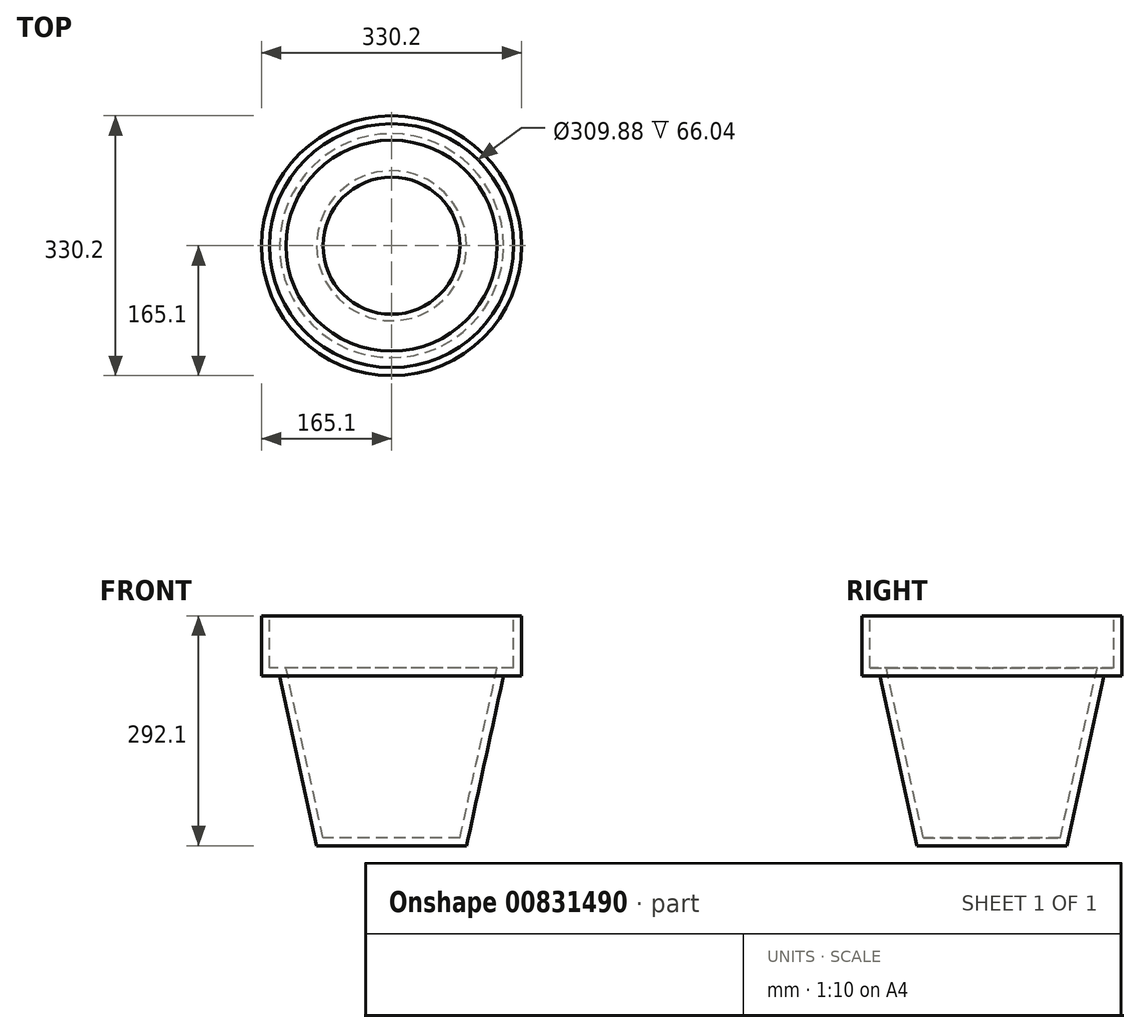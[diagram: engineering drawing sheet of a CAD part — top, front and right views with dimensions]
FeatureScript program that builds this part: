
annotation { "Feature Type Name" : "Feature", "Feature Type Description" : "" }
export const myFeature = defineFeature(function(context is Context, id is Id, definition is map)
    precondition{}
    {
        {
            var Q0;
            Q0=qCreatedBy(makeId("Front.planeOp"),FACE);
            var sketch = newSketch(context, id + "F0", { "sketchPlane" : qUnion([Q0])});
            skLineSegment(sketch, "E0", {"start": v(0, 0) * mm, "end": v(95.25, 0) * mm});
            skLineSegment(sketch, "E1", {"start": v(95.25, 0) * mm, "end": v(142.24, 215.9) * mm});
            skLineSegment(sketch, "E2", {"start": v(142.24, 215.9) * mm, "end": v(165.1, 215.9) * mm});
            skLineSegment(sketch, "E3", {"start": v(165.1, 215.9) * mm, "end": v(165.1, 292.1) * mm});
            skLineSegment(sketch, "E4", {"start": v(165.1, 292.1) * mm, "end": v(0, 292.1) * mm});
            skLineSegment(sketch, "E5", {"start": v(0, 292.1) * mm, "end": v(0, 0) * mm});
            skSolve(sketch);
        }
        {
            var Q0;
            Q0 = qSketchRegion(id + "F0", true);
            var Q1;
            Q1=sQuery(id+"F0.wireOp",EDGE,"E5");
            revolve(context, id + "F1", {"surfaceOperationType" : NewSurfaceOperationType.NEW, "entities" : qUnion([Q0]), "axis" : qUnion([Q1]), "revolveType" : RevolveType.FULL});
        }
        {
            var Q0;
            Q0=makeQuery(id+"F1.opRevolve","SWEPT_FACE",FACE,{"disambiguationData":[OSD([sQuery(id+"F0.wireOp",EDGE,"E4")])]});
            shell(context, id + "F2", {"entities" : qUnion([Q0]), "thickness" : 10.16 * mm});
        }
    });
